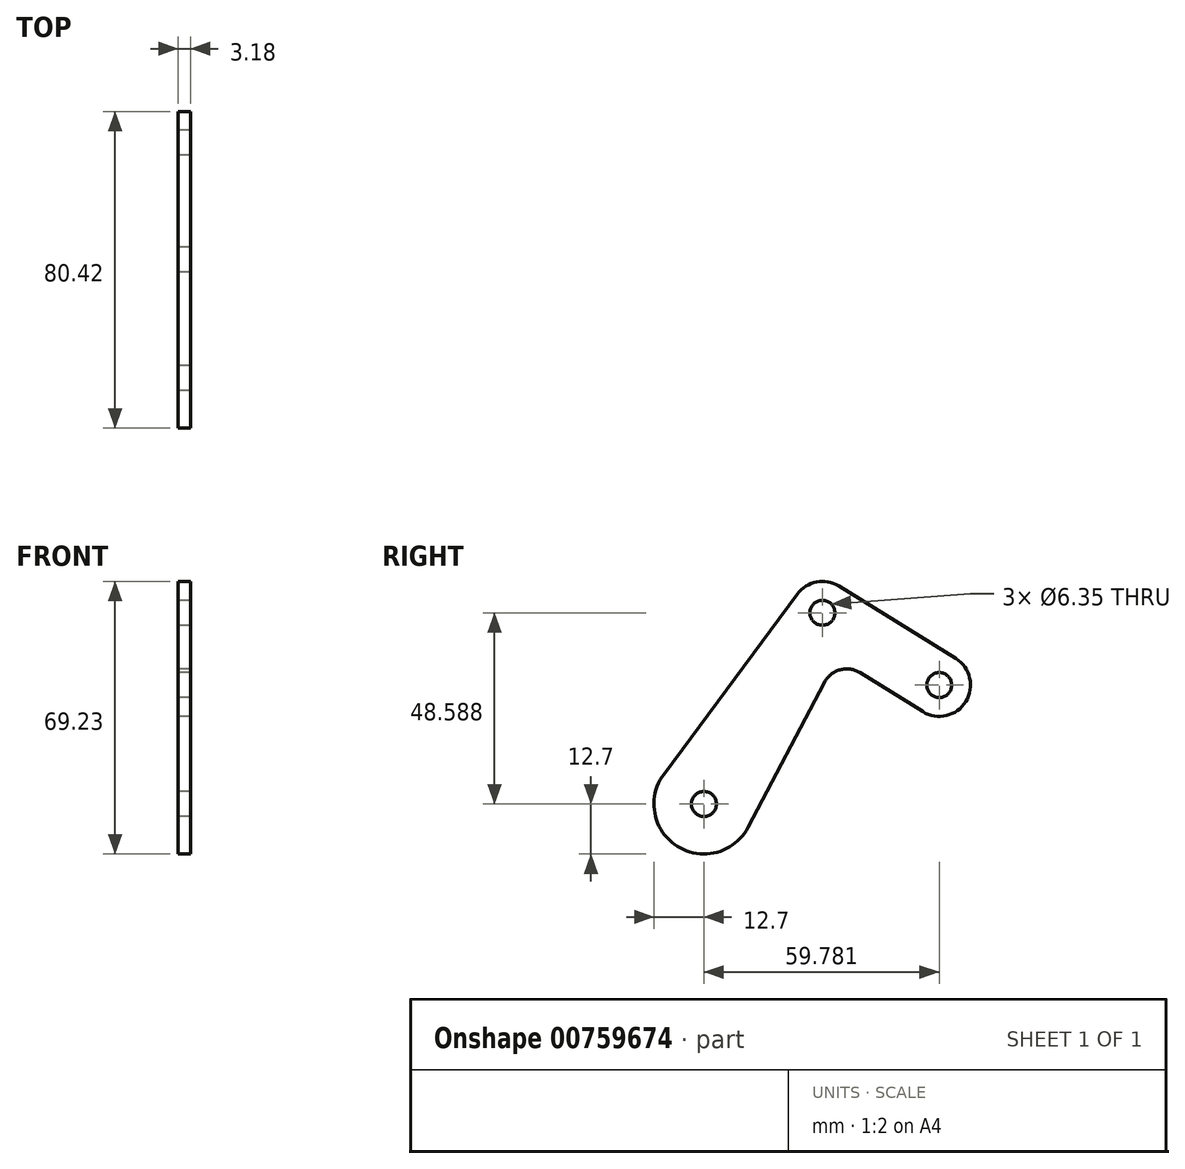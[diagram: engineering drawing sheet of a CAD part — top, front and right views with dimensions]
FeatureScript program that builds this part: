
annotation { "Feature Type Name" : "Feature", "Feature Type Description" : "" }
export const myFeature = defineFeature(function(context is Context, id is Id, definition is map)
    precondition{}
    {
        {
            var Q0;
            Q0=qCreatedBy(makeId("Right.planeOp"),FACE);
            var sketch = newSketch(context, id + "F0", { "sketchPlane" : qUnion([Q0])});
            skCircle(sketch, "E0", {"center": v(0, 0) * mm, "radius": 3.18 * mm});
            skCircle(sketch, "E1", {"center": v(30.09, 48.59) * mm, "radius": 3.18 * mm});
            skCircle(sketch, "E2", {"center": v(59.78, 30.2) * mm, "radius": 3.18 * mm});
            skArc(sketch, "E3", {"start": v(-10.2, 7.56) * mm, "mid": v(-6.76, -10.75) * mm, "end": v(11.24, -5.92) * mm});
            skArc(sketch, "E4", {"start": v(34.27, 55.34) * mm, "mid": v(28.6, 56.38) * mm, "end": v(23.71, 53.31) * mm});
            skArc(sketch, "E5", {"start": v(55.6, 23.45) * mm, "mid": v(66.53, 26.02) * mm, "end": v(63.96, 36.95) * mm});
            skLineSegment(sketch, "E6", {"start": v(-10.2, 7.56) * mm, "end": v(23.71, 53.31) * mm});
            skLineSegment(sketch, "E7", {"start": v(34.27, 55.34) * mm, "end": v(63.96, 36.95) * mm});
            skLineSegment(sketch, "E8", {"start": v(11.24, -5.92) * mm, "end": v(30.64, 30.92) * mm});
            skLineSegment(sketch, "E9", {"start": v(39.6, 33.36) * mm, "end": v(55.6, 23.45) * mm});
            skLineSegment(sketch, "E10", {"start": v(0, 0) * mm, "end": v(30.09, 48.59) * mm, "construction": true});
            skPoint(sketch, "E11.visualSharp", {"position": v(33.8, 36.95) * mm});
            skArc(sketch, "E11.filletArc", {"start": v(39.6, 33.36) * mm, "mid": v(34.59, 34.1) * mm, "end": v(30.64, 30.92) * mm});
            skLineSegment(sketch, "E12", {"start": v(30.09, 48.59) * mm, "end": v(59.78, 30.2) * mm, "construction": true});
            skSolve(sketch);
        }
        {
            var Q0;
            Q0=makeQuery(id+"F0.imprint","IMPRINT",FACE,{"disambiguationData":[TD([[makeQuery(id+"F0.imprint","IMPRINT",EDGE,{"derivedFrom":sQuery(id+"F0.wireOp",EDGE,"E0")}),-1.0]])]});
            extrude(context, id + "F1", {"entities" : qUnion([Q0]), "depth" : 3.17 * mm, "offsetDistance" : 25.4 * mm});
        }
    });
